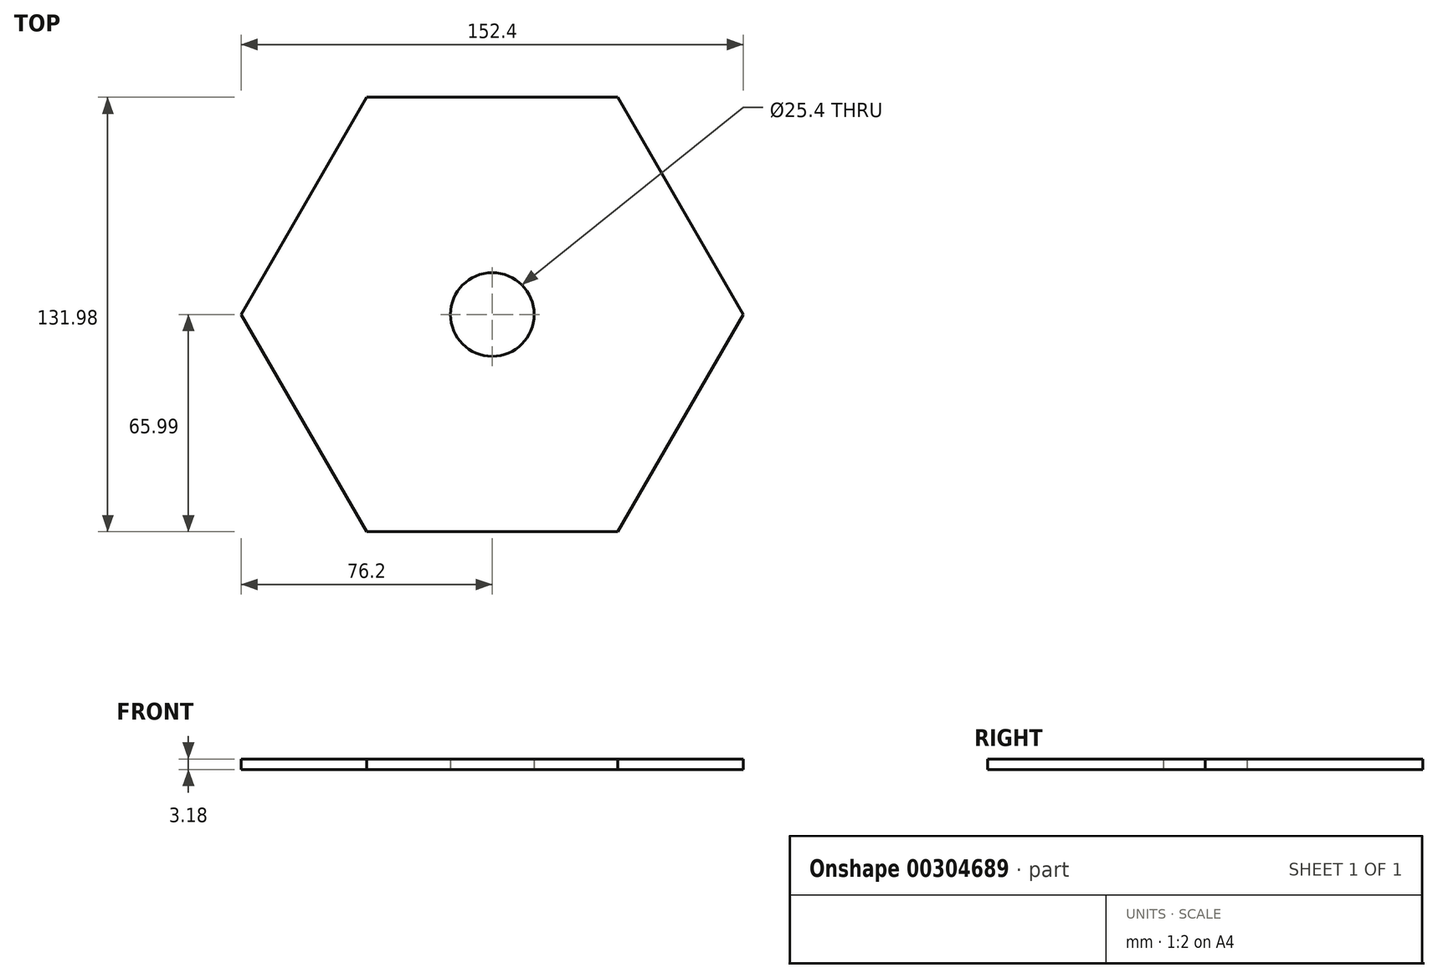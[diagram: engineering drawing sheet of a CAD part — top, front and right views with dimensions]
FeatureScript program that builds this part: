
annotation { "Feature Type Name" : "Feature", "Feature Type Description" : "" }
export const myFeature = defineFeature(function(context is Context, id is Id, definition is map)
    precondition{}
    {
        {
            var Q0;
            Q0=qCreatedBy(makeId("Top.planeOp"),FACE);
            var sketch = newSketch(context, id + "F0", { "sketchPlane" : qUnion([Q0])});
            skLineSegment(sketch, "E0", {"start": v(-76.2, 0) * mm, "end": v(0, 0) * mm, "construction": true});
            skLineSegment(sketch, "E1", {"start": v(0, 0) * mm, "end": v(76.2, 0) * mm, "construction": true});
            skLineSegment(sketch, "E2", {"start": v(0, 0) * mm, "end": v(38.1, 66) * mm, "construction": true});
            skLineSegment(sketch, "E3", {"start": v(-38.1, 66) * mm, "end": v(0, 0) * mm, "construction": true});
            skLineSegment(sketch, "E4", {"start": v(0, 0) * mm, "end": v(38.1, -66) * mm, "construction": true});
            skLineSegment(sketch, "E5", {"start": v(0, 0) * mm, "end": v(-38.1, -66) * mm, "construction": true});
            skLineSegment(sketch, "E6", {"start": v(-38.1, 66) * mm, "end": v(38.1, 66) * mm});
            skLineSegment(sketch, "E7", {"start": v(-38.1, 66) * mm, "end": v(-76.2, 0) * mm});
            skLineSegment(sketch, "E8", {"start": v(-76.2, 0) * mm, "end": v(-38.1, -66) * mm});
            skLineSegment(sketch, "E9", {"start": v(-38.1, -66) * mm, "end": v(38.1, -66) * mm});
            skLineSegment(sketch, "E10", {"start": v(38.1, -66) * mm, "end": v(76.2, 0) * mm});
            skLineSegment(sketch, "E11", {"start": v(38.1, 66) * mm, "end": v(76.2, 0) * mm});
            skCircle(sketch, "E12", {"center": v(0, 0) * mm, "radius": 12.7 * mm});
            skSolve(sketch);
        }
        {
            var Q0;
            Q0=makeQuery(id+"F0.imprint","IMPRINT",FACE,{"disambiguationData":[TD([[makeQuery(id+"F0.imprint","IMPRINT",EDGE,{"derivedFrom":sQuery(id+"F0.wireOp",EDGE,"E6")}),-1.0]])]});
            extrude(context, id + "F1", {"entities" : qUnion([Q0]), "endBound" : BoundingType.SYMMETRIC, "depth" : 3.17 * mm});
        }
    });
